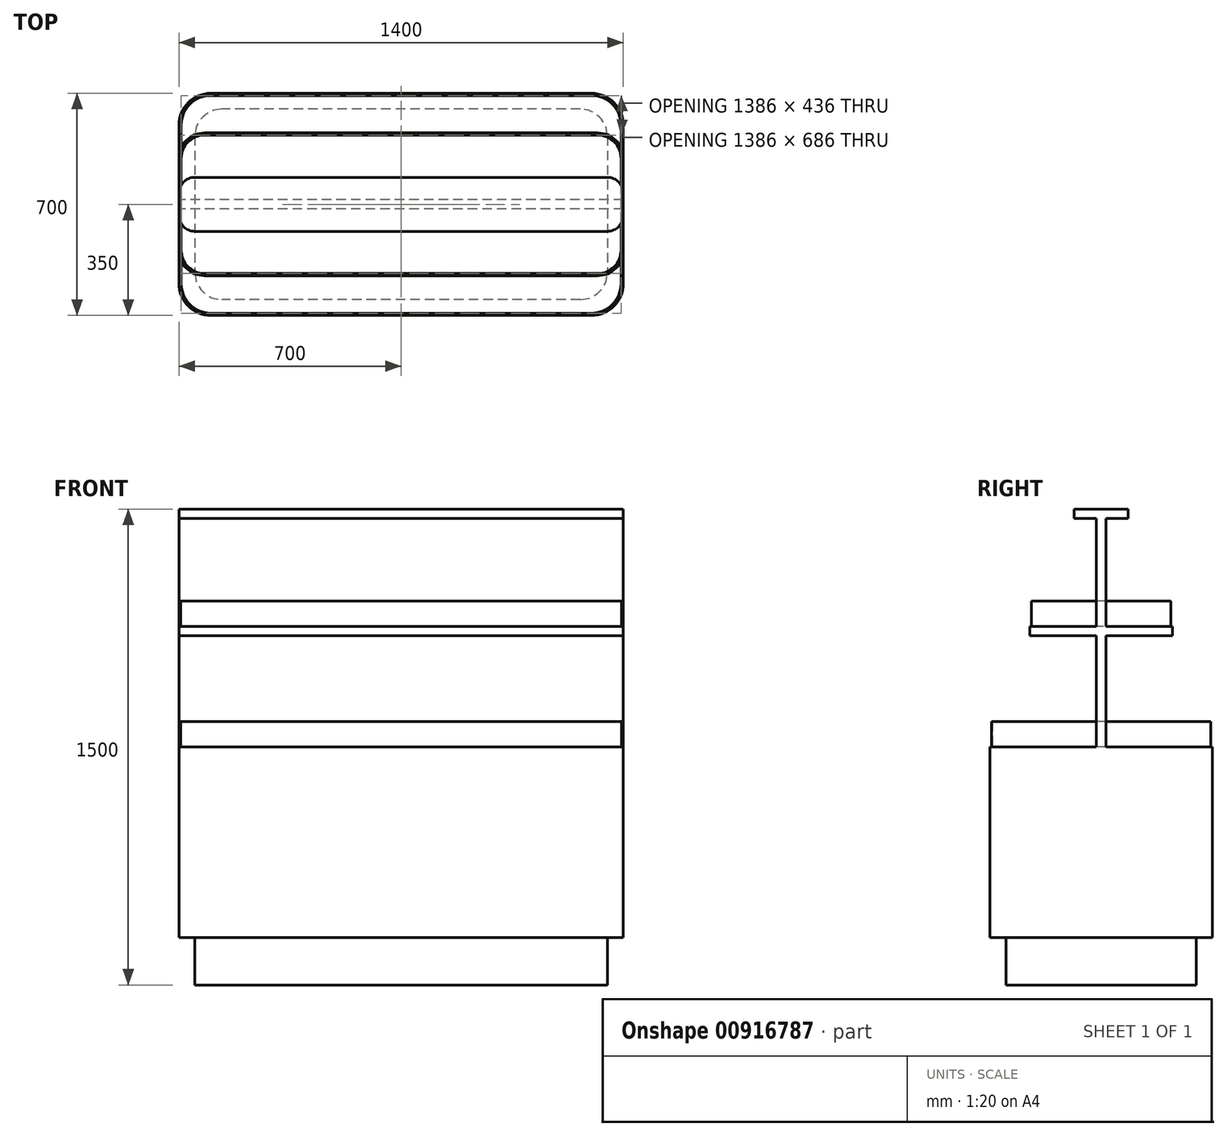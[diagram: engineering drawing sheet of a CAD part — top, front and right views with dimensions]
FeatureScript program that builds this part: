
annotation { "Feature Type Name" : "Feature", "Feature Type Description" : "" }
export const myFeature = defineFeature(function(context is Context, id is Id, definition is map)
    precondition{}
    {
        {
            var Q0;
            Q0=qCreatedBy(makeId("Front.planeOp"),FACE);
            var sketch = newSketch(context, id + "F0", { "sketchPlane" : qUnion([Q0])});
            skLineSegment(sketch, "E0.bottom", {"start": v(-700, 0) * mm, "end": v(700, 0) * mm});
            skLineSegment(sketch, "E0.top", {"start": v(-700, 1500) * mm, "end": v(700, 1500) * mm});
            skLineSegment(sketch, "E0.left", {"start": v(-700, 0) * mm, "end": v(-700, 1500) * mm});
            skLineSegment(sketch, "E0.right", {"start": v(700, 0) * mm, "end": v(700, 1500) * mm});
            skLineSegment(sketch, "E1", {"start": v(-700, 150) * mm, "end": v(700, 150) * mm});
            skLineSegment(sketch, "E2", {"start": v(-700, 750) * mm, "end": v(700, 750) * mm});
            skLineSegment(sketch, "E3", {"start": v(-700, 1470) * mm, "end": v(700, 1470) * mm});
            skLineSegment(sketch, "E4", {"start": v(-700, 1100) * mm, "end": v(700, 1100) * mm});
            skLineSegment(sketch, "E5", {"start": v(-700, 1130) * mm, "end": v(700, 1130) * mm});
            skSolve(sketch);
        }
        {
            var Q0;
            Q0=qCreatedBy(makeId("Top.planeOp"),FACE);
            var sketch = newSketch(context, id + "F1", { "sketchPlane" : qUnion([Q0])});
            skLineSegment(sketch, "E6.bottom", {"start": v(700, 350) * mm, "end": v(-700, 350) * mm});
            skLineSegment(sketch, "E6.top", {"start": v(700, -350) * mm, "end": v(-700, -350) * mm});
            skLineSegment(sketch, "E6.left", {"start": v(700, 350) * mm, "end": v(700, -350) * mm});
            skLineSegment(sketch, "E6.right", {"start": v(-700, 350) * mm, "end": v(-700, -350) * mm});
            skPoint(sketch, "E6.middle", {"position": v(0, 0) * mm});
            skLineSegment(sketch, "E7.bottom", {"start": v(700, 15) * mm, "end": v(-700, 15) * mm});
            skLineSegment(sketch, "E7.top", {"start": v(700, -15) * mm, "end": v(-700, -15) * mm});
            skLineSegment(sketch, "E7.left", {"start": v(700, 15) * mm, "end": v(700, -15) * mm});
            skLineSegment(sketch, "E7.right", {"start": v(-700, 15) * mm, "end": v(-700, -15) * mm});
            skLineSegment(sketch, "E8", {"start": v(-700, 225) * mm, "end": v(700, 225) * mm});
            skLineSegment(sketch, "E9", {"start": v(-700, -225) * mm, "end": v(700, -225) * mm});
            skLineSegment(sketch, "E10.0", {"start": v(650, 300) * mm, "end": v(-650, 300) * mm});
            skLineSegment(sketch, "E10.1", {"start": v(650, 300) * mm, "end": v(650, -300) * mm});
            skLineSegment(sketch, "E10.2", {"start": v(650, -300) * mm, "end": v(-650, -300) * mm});
            skLineSegment(sketch, "E10.3", {"start": v(-650, 300) * mm, "end": v(-650, -300) * mm});
            skLineSegment(sketch, "E11", {"start": v(-700, -85) * mm, "end": v(700, -85) * mm});
            skLineSegment(sketch, "E12", {"start": v(-700, 85) * mm, "end": v(700, 85) * mm});
            skSolve(sketch);
        }
        {
            var Q0;
            Q0=qCreatedBy(makeId("Top.planeOp"),FACE);
            var sketch = newSketch(context, id + "F2", { "sketchPlane" : qUnion([Q0])});
            skLineSegment(sketch, "E13.0", {"start": v(650, 300) * mm, "end": v(-650, 300) * mm});
            skLineSegment(sketch, "E13.1", {"start": v(-650, 300) * mm, "end": v(-650, -300) * mm});
            skLineSegment(sketch, "E13.2", {"start": v(650, -300) * mm, "end": v(-650, -300) * mm});
            skLineSegment(sketch, "E13.3", {"start": v(650, 300) * mm, "end": v(650, -300) * mm});
            skSolve(sketch);
        }
        {
            var Q0;
            Q0 = qSketchRegion(id + "F2", true);
            var Q1;
            Q1=sQuery(id+"F0.wireOp",VERTEX,"E1.end");
            extrude(context, id + "F3", {"entities" : qUnion([Q0]), "endBound" : BoundingType.UP_TO_VERTEX, "depth" : 25 * mm, "endBoundEntityVertex" : qUnion([Q1]), "offsetDistance" : 25 * mm});
        }
        {
            var Q0;
            Q0=makeQuery(id+"F3.opExtrude","CAP_FACE",FACE,{"disambiguationData":[OSD([sQuery(id+"F2.wireOp",EDGE,"E13.0"),sQuery(id+"F2.wireOp",EDGE,"E13.1"),sQuery(id+"F2.wireOp",EDGE,"E13.2"),sQuery(id+"F2.wireOp",EDGE,"E13.3")])],"isStart":false});
            var sketch = newSketch(context, id + "F4", { "sketchPlane" : qUnion([Q0])});
            skLineSegment(sketch, "E14.0", {"start": v(700, 350) * mm, "end": v(-700, 350) * mm});
            skLineSegment(sketch, "E14.1", {"start": v(-700, 350) * mm, "end": v(-700, -350) * mm});
            skLineSegment(sketch, "E14.2", {"start": v(700, -350) * mm, "end": v(-700, -350) * mm});
            skLineSegment(sketch, "E14.3", {"start": v(700, 350) * mm, "end": v(700, -350) * mm});
            skSolve(sketch);
        }
        {
            var Q0;
            Q0 = qSketchRegion(id + "F4", true);
            var Q1;
            Q1=sQuery(id+"F0.wireOp",VERTEX,"E2.end");
            extrude(context, id + "F5", {"entities" : qUnion([Q0]), "operationType" : NewBodyOperationType.ADD, "endBound" : BoundingType.UP_TO_VERTEX, "depth" : 25 * mm, "endBoundEntityVertex" : qUnion([Q1]), "offsetDistance" : 25 * mm});
        }
        {
            var Q0;
            Q0=makeQuery(id+"F5.opExtrude","CAP_FACE",FACE,{"disambiguationData":[OSD([sQuery(id+"F4.wireOp",EDGE,"E14.0"),sQuery(id+"F4.wireOp",EDGE,"E14.1"),sQuery(id+"F4.wireOp",EDGE,"E14.2"),sQuery(id+"F4.wireOp",EDGE,"E14.3")])],"isStart":false});
            var sketch = newSketch(context, id + "F6", { "sketchPlane" : qUnion([Q0])});
            skLineSegment(sketch, "E15.0", {"start": v(700, 15) * mm, "end": v(-700, 15) * mm});
            skLineSegment(sketch, "E15.1", {"start": v(700, -15) * mm, "end": v(-700, -15) * mm});
            skLineSegment(sketch, "E15.2", {"start": v(-700, 15) * mm, "end": v(-700, -15) * mm});
            skLineSegment(sketch, "E15.3", {"start": v(700, 15) * mm, "end": v(700, -15) * mm});
            skPoint(sketch, "E16.orphan", {"position": v(-700, 350) * mm});
            skPoint(sketch, "E17.orphan", {"position": v(-700, -350) * mm});
            skPoint(sketch, "E18.orphan", {"position": v(700, 350) * mm});
            skPoint(sketch, "E19.orphan", {"position": v(700, -350) * mm});
            skSolve(sketch);
        }
        {
            var Q0;
            Q0 = qSketchRegion(id + "F6", true);
            var Q1;
            Q1=sQuery(id+"F0.wireOp",VERTEX,"E0.top.start");
            extrude(context, id + "F7", {"entities" : qUnion([Q0]), "operationType" : NewBodyOperationType.ADD, "endBound" : BoundingType.UP_TO_VERTEX, "depth" : 25 * mm, "endBoundEntityVertex" : qUnion([Q1]), "offsetDistance" : 25 * mm});
        }
        {
            var Q0;
            Q0=qCreatedBy(makeId("Top.planeOp"),FACE);
            var Q1;
            Q1=sQuery(id+"F0.wireOp",VERTEX,"E4.start");
            cPlane(context, id + "F8", {"entities" : qUnion([Q0, Q1]), "cplaneType" : CPlaneType.PLANE_POINT, "offset" : 25 * mm, "width" : 150 * mm, "height" : 150 * mm});
        }
        {
            var Q0;
            Q0=qCreatedBy(id+"F8.planeOp",FACE);
            var sketch = newSketch(context, id + "F9", { "sketchPlane" : qUnion([Q0])});
            skLineSegment(sketch, "E20.0", {"start": v(-700, 225) * mm, "end": v(700, 225) * mm});
            skLineSegment(sketch, "E20.1", {"start": v(-700, -225) * mm, "end": v(700, -225) * mm});
            skLineSegment(sketch, "E21", {"start": v(-700, 225) * mm, "end": v(-700, -225) * mm});
            skLineSegment(sketch, "E22", {"start": v(700, -225) * mm, "end": v(700, 225) * mm});
            skSolve(sketch);
        }
        {
            var Q0;
            Q0 = qSketchRegion(id + "F9", true);
            var Q1;
            Q1=sQuery(id+"F0.wireOp",VERTEX,"E5.start");
            extrude(context, id + "F10", {"entities" : qUnion([Q0]), "operationType" : NewBodyOperationType.ADD, "endBound" : BoundingType.UP_TO_VERTEX, "depth" : 25 * mm, "endBoundEntityVertex" : qUnion([Q1]), "offsetDistance" : 25 * mm});
        }
        {
            var Q0;
            Q0=makeQuery(id+"F7.opExtrude","CAP_FACE",FACE,{"disambiguationData":[OSD([sQuery(id+"F6.wireOp",EDGE,"E15.0"),sQuery(id+"F6.wireOp",EDGE,"E15.1"),sQuery(id+"F6.wireOp",EDGE,"E15.2"),sQuery(id+"F6.wireOp",EDGE,"E15.3")])],"isStart":false});
            var sketch = newSketch(context, id + "F11", { "sketchPlane" : qUnion([Q0])});
            skLineSegment(sketch, "E23.0", {"start": v(-700, -85) * mm, "end": v(700, -85) * mm});
            skLineSegment(sketch, "E23.1", {"start": v(-700, 85) * mm, "end": v(700, 85) * mm});
            skLineSegment(sketch, "E24", {"start": v(-700, -85) * mm, "end": v(-700, 85) * mm});
            skLineSegment(sketch, "E25", {"start": v(700, -85) * mm, "end": v(700, 85) * mm});
            skSolve(sketch);
        }
        {
            var Q0;
            Q0 = qSketchRegion(id + "F11", true);
            var Q1;
            Q1=sQuery(id+"F0.wireOp",VERTEX,"E3.start");
            extrude(context, id + "F12", {"entities" : qUnion([Q0]), "operationType" : NewBodyOperationType.ADD, "endBound" : BoundingType.UP_TO_VERTEX, "oppositeDirection" : true, "depth" : 25 * mm, "endBoundEntityVertex" : qUnion([Q1]), "offsetDistance" : 25 * mm});
        }
        {
            var Q0;
            Q0=makeQuery(id+"F5.opExtrude","SWEPT_EDGE",EDGE,{"disambiguationData":[OSD([sQuery(id+"F4.wireOp",EDGE,"E14.2"),sQuery(id+"F4.wireOp",EDGE,"E14.3")])]});
            var Q1;
            Q1=makeQuery(id+"F5.opExtrude","SWEPT_EDGE",EDGE,{"disambiguationData":[OSD([sQuery(id+"F4.wireOp",EDGE,"E14.1"),sQuery(id+"F4.wireOp",EDGE,"E14.2")])]});
            var Q2;
            Q2=makeQuery(id+"F5.opExtrude","SWEPT_EDGE",EDGE,{"disambiguationData":[OSD([sQuery(id+"F4.wireOp",EDGE,"E14.0"),sQuery(id+"F4.wireOp",EDGE,"E14.3")])]});
            var Q3;
            Q3=makeQuery(id+"F5.opExtrude","SWEPT_EDGE",EDGE,{"disambiguationData":[OSD([sQuery(id+"F4.wireOp",EDGE,"E14.0"),sQuery(id+"F4.wireOp",EDGE,"E14.1")])]});
            fillet(context, id + "F13", {"entities" : qUnion([Q0, Q1, Q2, Q3]), "radius" : 100 * mm, "tangentPropagation" : true, "allowEdgeOverflow" : false});
        }
        {
            var Q0;
            Q0=makeQuery(id+"F3.opExtrude","SWEPT_EDGE",EDGE,{"disambiguationData":[OSD([sQuery(id+"F2.wireOp",EDGE,"E13.0"),sQuery(id+"F2.wireOp",EDGE,"E13.1")])]});
            var Q1;
            Q1=makeQuery(id+"F3.opExtrude","SWEPT_EDGE",EDGE,{"disambiguationData":[OSD([sQuery(id+"F2.wireOp",EDGE,"E13.1"),sQuery(id+"F2.wireOp",EDGE,"E13.2")])]});
            var Q2;
            Q2=makeQuery(id+"F3.opExtrude","SWEPT_EDGE",EDGE,{"disambiguationData":[OSD([sQuery(id+"F2.wireOp",EDGE,"E13.2"),sQuery(id+"F2.wireOp",EDGE,"E13.3")])]});
            var Q3;
            Q3=makeQuery(id+"F3.opExtrude","SWEPT_EDGE",EDGE,{"disambiguationData":[OSD([sQuery(id+"F2.wireOp",EDGE,"E13.0"),sQuery(id+"F2.wireOp",EDGE,"E13.3")])]});
            fillet(context, id + "F14", {"entities" : qUnion([Q0, Q1, Q2, Q3]), "radius" : 85 * mm, "tangentPropagation" : true, "allowEdgeOverflow" : false});
        }
        {
            var Q0;
            Q0=makeQuery(id+"F10.opExtrude","SWEPT_EDGE",EDGE,{"disambiguationData":[OSD([sQuery(id+"F9.wireOp",EDGE,"E20.0"),sQuery(id+"F9.wireOp",EDGE,"E22")])]});
            var Q1;
            Q1=makeQuery(id+"F10.opExtrude","SWEPT_EDGE",EDGE,{"disambiguationData":[OSD([sQuery(id+"F9.wireOp",EDGE,"E20.0"),sQuery(id+"F9.wireOp",EDGE,"E21")])]});
            var Q2;
            Q2=makeQuery(id+"F10.opExtrude","SWEPT_EDGE",EDGE,{"disambiguationData":[OSD([sQuery(id+"F9.wireOp",EDGE,"E20.1"),sQuery(id+"F9.wireOp",EDGE,"E21")])]});
            var Q3;
            Q3=makeQuery(id+"F10.opExtrude","SWEPT_EDGE",EDGE,{"disambiguationData":[OSD([sQuery(id+"F9.wireOp",EDGE,"E20.1"),sQuery(id+"F9.wireOp",EDGE,"E22")])]});
            fillet(context, id + "F15", {"entities" : qUnion([Q0, Q1, Q2, Q3]), "radius" : 80 * mm, "tangentPropagation" : true, "allowEdgeOverflow" : false});
        }
        {
            var Q0;
            Q0=makeQuery(id+"F12.opExtrude","SWEPT_EDGE",EDGE,{"disambiguationData":[OSD([sQuery(id+"F11.wireOp",EDGE,"E23.0"),sQuery(id+"F11.wireOp",EDGE,"E25")])]});
            var Q1;
            Q1=makeQuery(id+"F12.opExtrude","SWEPT_EDGE",EDGE,{"disambiguationData":[OSD([sQuery(id+"F11.wireOp",EDGE,"E23.1"),sQuery(id+"F11.wireOp",EDGE,"E25")])]});
            var Q2;
            Q2=makeQuery(id+"F12.opExtrude","SWEPT_EDGE",EDGE,{"disambiguationData":[OSD([sQuery(id+"F11.wireOp",EDGE,"E23.0"),sQuery(id+"F11.wireOp",EDGE,"E24")])]});
            var Q3;
            Q3=makeQuery(id+"F12.opExtrude","SWEPT_EDGE",EDGE,{"disambiguationData":[OSD([sQuery(id+"F11.wireOp",EDGE,"E23.1"),sQuery(id+"F11.wireOp",EDGE,"E24")])]});
            fillet(context, id + "F16", {"entities" : qUnion([Q0, Q1, Q2, Q3]), "radius" : 50 * mm, "tangentPropagation" : true, "allowEdgeOverflow" : false});
        }
        {
            var Q0;
            {var subQ0=sQuery(id+"F4.wireOp",EDGE,"E14.3");var subQ1=sQuery(id+"F4.wireOp",EDGE,"E14.2");var subQ2=sQuery(id+"F4.wireOp",EDGE,"E14.1");Q0=makeQuery(id+"F7.boolean.opBoolean","SPLIT",FACE,{"disambiguationData":[TD([makeQuery(id+"F5.opExtrude","SWEPT_FACE",FACE,{"disambiguationData":[OSD([subQ1])]})])],"derivedFrom":makeQuery(id+"F5.opExtrude","CAP_FACE",FACE,{"disambiguationData":[OSD([sQuery(id+"F4.wireOp",EDGE,"E14.0"),subQ2,subQ1,subQ0])],"isStart":false})});}
            var sketch = newSketch(context, id + "F17", { "sketchPlane" : qUnion([Q0])});
            skArc(sketch, "E26.0", {"start": v(-695, 250) * mm, "mid": v(-667.18, 317.18) * mm, "end": v(-600, 345) * mm});
            skLineSegment(sketch, "E26.1", {"start": v(600, 345) * mm, "end": v(-600, 345) * mm});
            skLineSegment(sketch, "E26.2", {"start": v(-695, 250) * mm, "end": v(-695, -250) * mm});
            skArc(sketch, "E26.3", {"start": v(600, 345) * mm, "mid": v(667.18, 317.18) * mm, "end": v(695, 250) * mm});
            skArc(sketch, "E26.4", {"start": v(-600, -345) * mm, "mid": v(-667.18, -317.18) * mm, "end": v(-695, -250) * mm});
            skLineSegment(sketch, "E26.5", {"start": v(600, -345) * mm, "end": v(-600, -345) * mm});
            skArc(sketch, "E26.6", {"start": v(695, -250) * mm, "mid": v(667.18, -317.18) * mm, "end": v(600, -345) * mm});
            skLineSegment(sketch, "E26.7", {"start": v(695, 250) * mm, "end": v(695, -250) * mm});
            skLineSegment(sketch, "E27.0", {"start": v(600, -343) * mm, "end": v(-600, -343) * mm});
            skArc(sketch, "E27.1", {"start": v(693, -250) * mm, "mid": v(665.76, -315.76) * mm, "end": v(600, -343) * mm});
            skArc(sketch, "E27.2", {"start": v(-600, -343) * mm, "mid": v(-665.76, -315.76) * mm, "end": v(-693, -250) * mm});
            skLineSegment(sketch, "E27.3", {"start": v(693, 250) * mm, "end": v(693, -250) * mm});
            skLineSegment(sketch, "E27.4", {"start": v(-693, 250) * mm, "end": v(-693, -250) * mm});
            skArc(sketch, "E27.5", {"start": v(-693, 250) * mm, "mid": v(-665.76, 315.76) * mm, "end": v(-600, 343) * mm});
            skLineSegment(sketch, "E27.6", {"start": v(600, 343) * mm, "end": v(-600, 343) * mm});
            skArc(sketch, "E27.7", {"start": v(600, 343) * mm, "mid": v(665.76, 315.76) * mm, "end": v(693, 250) * mm});
            skSolve(sketch);
        }
        {
            var Q0;
            Q0 = qSketchRegion(id + "F17", true);
            extrude(context, id + "F18", {"entities" : qUnion([Q0]), "depth" : 80 * mm, "offsetDistance" : 25 * mm});
        }
        {
            var Q0;
            {var subQ0=sQuery(id+"F9.wireOp",EDGE,"E20.1");var subQ1=sQuery(id+"F9.wireOp",EDGE,"E21");var subQ2=sQuery(id+"F9.wireOp",EDGE,"E22");Q0=makeQuery(id+"F10.boolean.opBoolean","SPLIT",FACE,{"disambiguationData":[TD([makeQuery(id+"F7.opExtrude","SWEPT_FACE",FACE,{"disambiguationData":[OSD([sQuery(id+"F6.wireOp",EDGE,"E15.1")])]})])],"derivedFrom":makeQuery(id+"F10.opExtrude","CAP_FACE",FACE,{"disambiguationData":[OSD([sQuery(id+"F9.wireOp",EDGE,"E20.0"),subQ0,subQ1,subQ2])],"isStart":false})});}
            var sketch = newSketch(context, id + "F19", { "sketchPlane" : qUnion([Q0])});
            skLineSegment(sketch, "E28.0", {"start": v(-695, 145) * mm, "end": v(-695, 15) * mm});
            skLineSegment(sketch, "E28.1", {"start": v(695, 15) * mm, "end": v(695, 145) * mm});
            skArc(sketch, "E28.2", {"start": v(695, 145) * mm, "mid": v(673.03, 198.03) * mm, "end": v(620, 220) * mm});
            skLineSegment(sketch, "E28.3", {"start": v(-620, 220) * mm, "end": v(620, 220) * mm});
            skArc(sketch, "E28.4", {"start": v(-620, 220) * mm, "mid": v(-673.03, 198.03) * mm, "end": v(-695, 145) * mm});
            skLineSegment(sketch, "E29.0", {"start": v(695, -145) * mm, "end": v(695, -15) * mm});
            skLineSegment(sketch, "E29.1", {"start": v(-695, -15) * mm, "end": v(-695, -145) * mm});
            skArc(sketch, "E29.2", {"start": v(-695, -145) * mm, "mid": v(-673.03, -198.03) * mm, "end": v(-620, -220) * mm});
            skLineSegment(sketch, "E29.3", {"start": v(-620, -220) * mm, "end": v(620, -220) * mm});
            skArc(sketch, "E29.4", {"start": v(620, -220) * mm, "mid": v(673.03, -198.03) * mm, "end": v(695, -145) * mm});
            skLineSegment(sketch, "E30", {"start": v(-695, 15) * mm, "end": v(-695, -15) * mm});
            skLineSegment(sketch, "E31", {"start": v(695, 15) * mm, "end": v(695, -15) * mm});
            skLineSegment(sketch, "E32.0", {"start": v(693, 15) * mm, "end": v(693, 145) * mm});
            skLineSegment(sketch, "E32.1", {"start": v(-693, 15) * mm, "end": v(-693, -15) * mm});
            skLineSegment(sketch, "E32.2", {"start": v(-693, 145) * mm, "end": v(-693, 15) * mm});
            skArc(sketch, "E32.3", {"start": v(-620, 218) * mm, "mid": v(-671.62, 196.62) * mm, "end": v(-693, 145) * mm});
            skLineSegment(sketch, "E32.4", {"start": v(-620, 218) * mm, "end": v(620, 218) * mm});
            skLineSegment(sketch, "E32.5", {"start": v(-693, -15) * mm, "end": v(-693, -145) * mm});
            skArc(sketch, "E32.6", {"start": v(693, 145) * mm, "mid": v(671.62, 196.62) * mm, "end": v(620, 218) * mm});
            skArc(sketch, "E32.7", {"start": v(-693, -145) * mm, "mid": v(-671.62, -196.62) * mm, "end": v(-620, -218) * mm});
            skLineSegment(sketch, "E32.8", {"start": v(-620, -218) * mm, "end": v(620, -218) * mm});
            skArc(sketch, "E32.9", {"start": v(620, -218) * mm, "mid": v(671.62, -196.62) * mm, "end": v(693, -145) * mm});
            skLineSegment(sketch, "E32.10", {"start": v(693, -145) * mm, "end": v(693, -15) * mm});
            skLineSegment(sketch, "E32.11", {"start": v(693, 15) * mm, "end": v(693, -15) * mm});
            skSolve(sketch);
        }
        {
            var Q0;
            Q0 = qSketchRegion(id + "F19", true);
            extrude(context, id + "F20", {"entities" : qUnion([Q0]), "depth" : 80 * mm, "offsetDistance" : 25 * mm});
        }
    });
